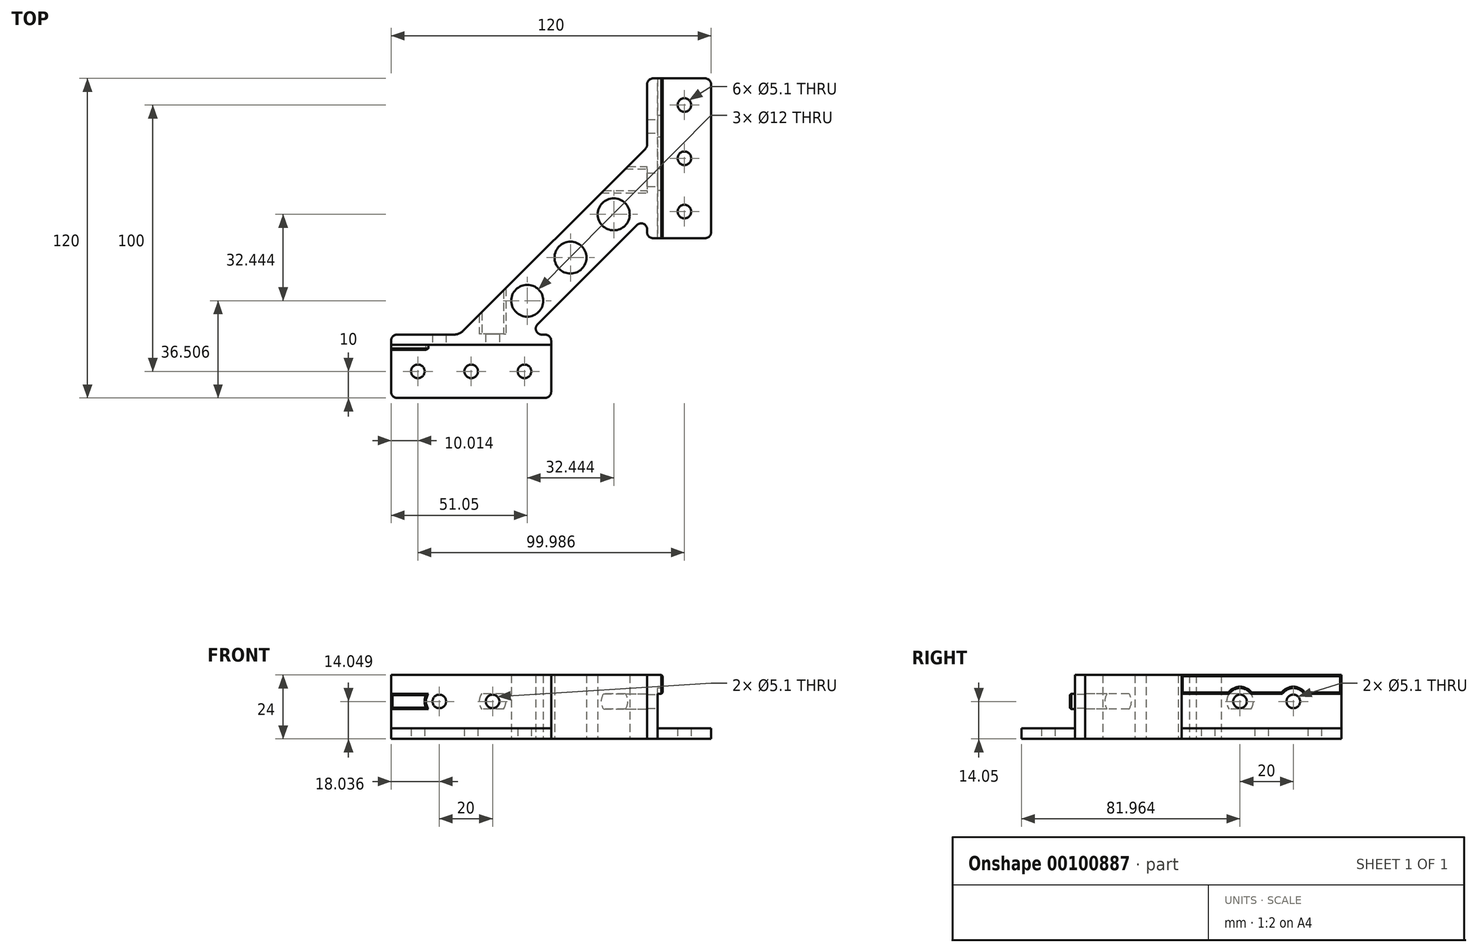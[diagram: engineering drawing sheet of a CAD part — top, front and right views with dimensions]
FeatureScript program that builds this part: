
annotation { "Feature Type Name" : "Feature", "Feature Type Description" : "" }
export const myFeature = defineFeature(function(context is Context, id is Id, definition is map)
    precondition{}
    {
        {
            var Q0;
            Q0=qCreatedBy(makeId("Top.planeOp"),FACE);
            var sketch = newSketch(context, id + "F0", { "sketchPlane" : qUnion([Q0])});
            skLineSegment(sketch, "E0", {"start": v(72.19, 64.92) * mm, "end": v(34.9, 27.62) * mm});
            skLineSegment(sketch, "E1", {"start": v(75.35, 93.53) * mm, "end": v(7.1, 25.27) * mm});
            skLineSegment(sketch, "E2", {"start": v(90, 80) * mm, "end": v(90, 70) * mm, "construction": true});
            skLineSegment(sketch, "E3", {"start": v(90, 80) * mm, "end": v(90, 90) * mm, "construction": true});
            skCircle(sketch, "E4", {"center": v(90, 90) * mm, "radius": 2.55 * mm});
            skCircle(sketch, "E5", {"center": v(90, 70) * mm, "radius": 2.55 * mm});
            skLineSegment(sketch, "E6", {"start": v(20.01, 10) * mm, "end": v(10.01, 10) * mm, "construction": true});
            skLineSegment(sketch, "E7", {"start": v(20.01, 10) * mm, "end": v(30.01, 10) * mm, "construction": true});
            skCircle(sketch, "E8", {"center": v(30.01, 10) * mm, "radius": 2.55 * mm});
            skCircle(sketch, "E9", {"center": v(10.01, 10) * mm, "radius": 2.55 * mm});
            skLineSegment(sketch, "E10", {"start": v(80, 92.8) * mm, "end": v(80, 73.96) * mm});
            skLineSegment(sketch, "E11", {"start": v(7.2, 20) * mm, "end": v(26.04, 20) * mm});
            skCircle(sketch, "E12", {"center": v(31.05, 36.5) * mm, "radius": 6 * mm});
            skCircle(sketch, "E13", {"center": v(63.5, 68.95) * mm, "radius": 6 * mm});
            skCircle(sketch, "E14", {"center": v(47.27, 52.73) * mm, "radius": 6 * mm});
            skPoint(sketch, "E15.visualSharp", {"position": v(0, 0) * mm});
            skPoint(sketch, "E16.visualSharp", {"position": v(40, 0) * mm});
            skArc(sketch, "E16.filletArc", {"start": v(37.77, 0) * mm, "mid": v(39.35, 0.65) * mm, "end": v(40, 2.23) * mm});
            skPoint(sketch, "E17.visualSharp", {"position": v(40, 20) * mm});
            skPoint(sketch, "E18.visualSharp", {"position": v(100, 60) * mm});
            skArc(sketch, "E18.filletArc", {"start": v(97.77, 60) * mm, "mid": v(99.35, 60.65) * mm, "end": v(100, 62.23) * mm});
            skPoint(sketch, "E19.visualSharp", {"position": v(80, 60) * mm});
            skArc(sketch, "E20.filletArc", {"start": v(79.42, 72.46) * mm, "mid": v(79.85, 73.16) * mm, "end": v(80, 73.96) * mm});
            skLineSegment(sketch, "E21", {"start": v(80, 60) * mm, "end": v(40, 20) * mm, "construction": true});
            skLineSegment(sketch, "E22", {"start": v(63.5, 68.95) * mm, "end": v(57.13, 75.31) * mm, "construction": true});
            skLineSegment(sketch, "E23", {"start": v(47.27, 52.73) * mm, "end": v(40.9, 59.1) * mm, "construction": true});
            skLineSegment(sketch, "E24", {"start": v(31.05, 36.5) * mm, "end": v(24.69, 42.87) * mm, "construction": true});
            skLineSegment(sketch, "E25", {"start": v(40, 0) * mm, "end": v(-17.77, 0) * mm});
            skLineSegment(sketch, "E26", {"start": v(-20, 2.23) * mm, "end": v(-20, 20) * mm});
            skLineSegment(sketch, "E27", {"start": v(-20, 20) * mm, "end": v(7.2, 20) * mm});
            skLineSegment(sketch, "E28", {"start": v(10.01, 10) * mm, "end": v(-9.99, 10) * mm, "construction": true});
            skCircle(sketch, "E29", {"center": v(-9.99, 10) * mm, "radius": 2.55 * mm});
            skLineSegment(sketch, "E30", {"start": v(3.56, 23.8) * mm, "end": v(-17.77, 23.8) * mm});
            skLineSegment(sketch, "E31", {"start": v(-20, 21.58) * mm, "end": v(-20, 20) * mm});
            skArc(sketch, "E32.filletArc", {"start": v(3.56, 23.8) * mm, "mid": v(5.47, 24.2) * mm, "end": v(7.1, 25.27) * mm});
            skPoint(sketch, "E33.visualSharp", {"position": v(-20, 23.8) * mm});
            skArc(sketch, "E33.filletArc", {"start": v(-17.77, 23.8) * mm, "mid": v(-19.35, 23.16) * mm, "end": v(-20, 21.58) * mm});
            skPoint(sketch, "E34.visualSharp", {"position": v(-20, 0) * mm});
            skArc(sketch, "E34.filletArc", {"start": v(-20, 2.23) * mm, "mid": v(-19.35, 0.65) * mm, "end": v(-17.77, 0) * mm});
            skLineSegment(sketch, "E35", {"start": v(36.47, 23.8) * mm, "end": v(37.77, 23.8) * mm});
            skLineSegment(sketch, "E36", {"start": v(40, 2.23) * mm, "end": v(40, 21.58) * mm});
            skPoint(sketch, "E37.visualSharp", {"position": v(40, 23.8) * mm});
            skArc(sketch, "E37.filletArc", {"start": v(40, 21.58) * mm, "mid": v(39.35, 23.16) * mm, "end": v(37.77, 23.8) * mm});
            skArc(sketch, "E38.filletArc", {"start": v(34.9, 27.62) * mm, "mid": v(34.4, 25.19) * mm, "end": v(36.47, 23.8) * mm});
            skLineSegment(sketch, "E39", {"start": v(40, 20) * mm, "end": v(26.04, 20) * mm});
            skLineSegment(sketch, "E40", {"start": v(97.77, 120) * mm, "end": v(82.23, 120) * mm});
            skLineSegment(sketch, "E41", {"start": v(80, 117.77) * mm, "end": v(80, 92.8) * mm});
            skLineSegment(sketch, "E42", {"start": v(80, 120) * mm, "end": v(78.23, 120) * mm});
            skLineSegment(sketch, "E43", {"start": v(76, 117.77) * mm, "end": v(76, 95.1) * mm});
            skLineSegment(sketch, "E44", {"start": v(100, 117.77) * mm, "end": v(100, 62.23) * mm});
            skPoint(sketch, "E45.visualSharp", {"position": v(100, 120) * mm});
            skArc(sketch, "E45.filletArc", {"start": v(100, 117.77) * mm, "mid": v(99.35, 119.35) * mm, "end": v(97.77, 120) * mm});
            skPoint(sketch, "E46.visualSharp", {"position": v(80, 120) * mm});
            skPoint(sketch, "E47.visualSharp", {"position": v(76, 120) * mm});
            skArc(sketch, "E47.filletArc", {"start": v(78.23, 120) * mm, "mid": v(76.65, 119.35) * mm, "end": v(76, 117.77) * mm});
            skPoint(sketch, "E48.newPointB", {"position": v(76.2, 94.37) * mm});
            skArc(sketch, "E48.filletArc", {"start": v(75.35, 93.53) * mm, "mid": v(75.83, 94.25) * mm, "end": v(76, 95.1) * mm});
            skLineSegment(sketch, "E49", {"start": v(80, 120) * mm, "end": v(82.23, 120) * mm});
            skLineSegment(sketch, "E50", {"start": v(80, 117.77) * mm, "end": v(80, 120) * mm});
            skLineSegment(sketch, "E51", {"start": v(90, 90) * mm, "end": v(90, 110) * mm, "construction": true});
            skCircle(sketch, "E52", {"center": v(90, 110) * mm, "radius": 2.55 * mm});
            skLineSegment(sketch, "E53", {"start": v(97.77, 60) * mm, "end": v(78.23, 60) * mm});
            skLineSegment(sketch, "E54", {"start": v(76, 62.23) * mm, "end": v(76, 63.34) * mm});
            skPoint(sketch, "E55.visualSharp", {"position": v(76, 60) * mm});
            skArc(sketch, "E55.filletArc", {"start": v(76, 62.23) * mm, "mid": v(76.65, 60.65) * mm, "end": v(78.23, 60) * mm});
            skLineSegment(sketch, "E56", {"start": v(80, 73.96) * mm, "end": v(80, 60) * mm});
            skArc(sketch, "E57.filletArc", {"start": v(76, 63.34) * mm, "mid": v(74.62, 65.4) * mm, "end": v(72.19, 64.92) * mm});
            skSolve(sketch);
        }
        {
            var Q0;
            Q0=makeQuery(id+"F0.imprint","IMPRINT",FACE,{"disambiguationData":[TD([[makeQuery(id+"F0.imprint","IMPRINT",EDGE,{"derivedFrom":sQuery(id+"F0.wireOp",EDGE,"vu9Mk9B3-tYnc-hBh3-YSRa-gffN2kaJFWOu.bottom")}),1.0]])]});
            var Q1;
            Q1=makeQuery(id+"F0.imprint","IMPRINT",FACE,{"disambiguationData":[TD([[makeQuery(id+"F0.imprint","IMPRINT",EDGE,{"derivedFrom":sQuery(id+"F0.wireOp",EDGE,"dHSvPDMb-Tlqj-Q4RQ-VTB6-cDBXFjwvFFpO.bottom")}),1.0]])]});
            var Q2;
            Q2=makeQuery(id+"F0.imprint","IMPRINT",FACE,{"disambiguationData":[TD([[makeQuery(id+"F0.imprint","IMPRINT",EDGE,{"derivedFrom":sQuery(id+"F0.wireOp",EDGE,"vu9Mk9B3-tYnc-hBh3-YSRa-gffN2kaJFWOu.top")}),-1.0]])]});
            var Q3;
            Q3=makeQuery(id+"F0.imprint","IMPRINT",FACE,{"disambiguationData":[TD([[makeQuery(id+"F0.imprint","IMPRINT",EDGE,{"derivedFrom":sQuery(id+"F0.wireOp",EDGE,"dfbe4f2e-9168-4a66-9229-19b176851153.filletArc")}),-1.0]])]});
            var Q4;
            Q4=makeQuery(id+"F0.imprint","IMPRINT",FACE,{"disambiguationData":[TD([[makeQuery(id+"F0.imprint","IMPRINT",EDGE,{"derivedFrom":sQuery(id+"F0.wireOp",EDGE,"E8")}),-1.0]])]});
            var Q5;
            Q5=makeQuery(id+"F0.imprint","IMPRINT",FACE,{"disambiguationData":[TD([[makeQuery(id+"F0.imprint","IMPRINT",EDGE,{"derivedFrom":sQuery(id+"F0.wireOp",EDGE,"dHSvPDMb-Tlqj-Q4RQ-VTB6-cDBXFjwvFFpO.top")}),-1.0]])]});
            var Q6;
            Q6=makeQuery(id+"F0.imprint","IMPRINT",FACE,{"disambiguationData":[TD([[makeQuery(id+"F0.imprint","IMPRINT",EDGE,{"derivedFrom":sQuery(id+"F0.wireOp",EDGE,"d131ca40-41fb-4f96-a70f-9a93196c1724.filletArc")}),-1.0]])]});
            var Q7;
            Q7=makeQuery(id+"F0.imprint","IMPRINT",FACE,{"disambiguationData":[TD([[makeQuery(id+"F0.imprint","IMPRINT",EDGE,{"derivedFrom":sQuery(id+"F0.wireOp",EDGE,"E4")}),-1.0]])]});
            extrude(context, id + "F1", {"entities" : qUnion([Q0, Q1, Q2, Q3, Q4, Q5, Q6, Q7]), "depth" : 4 * mm});
        }
        {
            var Q0;
            Q0=makeQuery(id+"F0.imprint","IMPRINT",FACE,{"disambiguationData":[TD([[makeQuery(id+"F0.imprint","IMPRINT",EDGE,{"derivedFrom":sQuery(id+"F0.wireOp",EDGE,"E0")}),-1.0]])]});
            var Q1;
            Q1=makeQuery(id+"F0.imprint","IMPRINT",FACE,{"disambiguationData":[TD([[makeQuery(id+"F0.imprint","IMPRINT",EDGE,{"derivedFrom":sQuery(id+"F0.wireOp",EDGE,"dfbe4f2e-9168-4a66-9229-19b176851153.filletArc")}),-1.0]])]});
            var Q2;
            Q2=makeQuery(id+"F0.imprint","IMPRINT",FACE,{"disambiguationData":[TD([[makeQuery(id+"F0.imprint","IMPRINT",EDGE,{"derivedFrom":sQuery(id+"F0.wireOp",EDGE,"E35")}),-1.0]])]});
            var Q3;
            Q3=makeQuery(id+"F0.imprint","IMPRINT",FACE,{"disambiguationData":[TD([[makeQuery(id+"F0.imprint","IMPRINT",EDGE,{"derivedFrom":sQuery(id+"F0.wireOp",EDGE,"d131ca40-41fb-4f96-a70f-9a93196c1724.filletArc")}),-1.0]])]});
            extrude(context, id + "F2", {"entities" : qUnion([Q0, Q1, Q2, Q3]), "depth" : 24 * mm});
        }
        {
            var Q0;
            Q0=makeQuery(id+"F2.opExtrude","SWEPT_FACE",FACE,{"disambiguationData":[OSD([sQuery(id+"F0.wireOp",EDGE,"E10")])]});
            var sketch = newSketch(context, id + "F3", { "sketchPlane" : qUnion([Q0])});
            skCircle(sketch, "E58", {"center": v(81.96, 14.05) * mm, "radius": 2.55 * mm});
            skCircle(sketch, "E59", {"center": v(81.96, 14.05) * mm, "radius": 5 * mm});
            skLineSegment(sketch, "E60", {"start": v(75.68, 14.05) * mm, "end": v(75.68, 16.95) * mm, "construction": true});
            skLineSegment(sketch, "E61", {"start": v(75.68, 14.05) * mm, "end": v(75.68, 11.15) * mm, "construction": true});
            skLineSegment(sketch, "E62.bottom", {"start": v(84.86, 11.15) * mm, "end": v(79.06, 11.15) * mm});
            skLineSegment(sketch, "E62.top", {"start": v(84.86, 16.95) * mm, "end": v(79.06, 16.95) * mm});
            skLineSegment(sketch, "E62.left", {"start": v(84.86, 11.15) * mm, "end": v(84.86, 16.95) * mm});
            skLineSegment(sketch, "E62.right", {"start": v(79.06, 11.15) * mm, "end": v(79.06, 16.95) * mm});
            skLineSegment(sketch, "E63", {"start": v(60, 16.95) * mm, "end": v(120, 16.95) * mm});
            skLineSegment(sketch, "E64", {"start": v(60, 11.15) * mm, "end": v(120, 11.15) * mm});
            skLineSegment(sketch, "E65", {"start": v(81.96, 14.05) * mm, "end": v(101.96, 14.05) * mm, "construction": true});
            skLineSegment(sketch, "E66", {"start": v(81.96, 14.05) * mm, "end": v(60, 14.05) * mm, "construction": true});
            skCircle(sketch, "E67", {"center": v(101.96, 14.05) * mm, "radius": 2.55 * mm});
            skLineSegment(sketch, "E68.bottom", {"start": v(104.86, 11.15) * mm, "end": v(99.06, 11.15) * mm});
            skLineSegment(sketch, "E68.top", {"start": v(104.86, 16.95) * mm, "end": v(99.06, 16.95) * mm});
            skLineSegment(sketch, "E68.left", {"start": v(104.86, 11.15) * mm, "end": v(104.86, 16.95) * mm});
            skLineSegment(sketch, "E68.right", {"start": v(99.06, 11.15) * mm, "end": v(99.06, 16.95) * mm});
            skCircle(sketch, "E69", {"center": v(101.96, 14.05) * mm, "radius": 5 * mm});
            skSolve(sketch);
        }
        {
            var Q0;
            Q0=makeQuery(id+"F3.imprint","IMPRINT",FACE,{"disambiguationData":[TD([[makeQuery(id+"F3.imprint","IMPRINT",EDGE,{"derivedFrom":sQuery(id+"F3.wireOp",EDGE,"E58")}),1.0]])]});
            var Q1;
            Q1=makeQuery(id+"F3.imprint","IMPRINT",FACE,{"disambiguationData":[TD([[makeQuery(id+"F3.imprint","IMPRINT",EDGE,{"derivedFrom":sQuery(id+"F3.wireOp",EDGE,"E67")}),1.0]])]});
            extrude(context, id + "F4", {"entities" : qUnion([Q0, Q1]), "operationType" : NewBodyOperationType.REMOVE, "oppositeDirection" : true, "depth" : 25 * mm});
        }
        {
            var Q0;
            Q0=makeQuery(id+"F3.imprint","IMPRINT",FACE,{"disambiguationData":[TD([[makeQuery(id+"F3.imprint","IMPRINT",EDGE,{"derivedFrom":sQuery(id+"F3.wireOp",EDGE,"E58")}),-1.0]])]});
            var Q1;
            {var subQ0=sQuery(id+"F3.wireOp",EDGE,"jhnVX4wI-j8lZ-3AVm-xeLm-CdO5rJdbQkBP");var subQ1=sQuery(id+"F3.wireOp",EDGE,"E59");var subQ2=makeQuery(id+"F3.imprint","INTERSECT",VERTEX,{"disambiguationData":[OD(0.0)],"derivedFrom":[subQ1,subQ0]});Q1=makeQuery(id+"F3.imprint","IMPRINT",FACE,{"disambiguationData":[TD([[makeQuery(id+"F3.imprint","IMPRINT",EDGE,{"disambiguationData":[TD([[subQ2,1.0]])],"derivedFrom":subQ1}),1.0]])]});}
            var Q2;
            {var subQ0=sQuery(id+"F3.wireOp",EDGE,"Id8RdnPz-wRiC-AdUC-IpGY-bHKos9TCPgaF");var subQ1=sQuery(id+"F3.wireOp",EDGE,"E59");var subQ2=makeQuery(id+"F3.imprint","INTERSECT",VERTEX,{"disambiguationData":[OD(0.0)],"derivedFrom":[subQ1,subQ0]});Q2=makeQuery(id+"F3.imprint","IMPRINT",FACE,{"disambiguationData":[TD([[makeQuery(id+"F3.imprint","IMPRINT",EDGE,{"disambiguationData":[TD([[subQ2,-1.0]])],"derivedFrom":subQ1}),1.0]])]});}
            var Q3;
            {var subQ5=sQuery(id+"F3.wireOp",EDGE,"E62.right");Q3=makeQuery(id+"F3.imprint","IMPRINT",FACE,{"disambiguationData":[TD([[makeQuery(id+"F3.imprint","IMPRINT",EDGE,{"derivedFrom":subQ5}),1.0]])]});}
            var Q4;
            {var subQ5=sQuery(id+"F3.wireOp",EDGE,"E62.left");Q4=makeQuery(id+"F3.imprint","IMPRINT",FACE,{"disambiguationData":[TD([[makeQuery(id+"F3.imprint","IMPRINT",EDGE,{"derivedFrom":subQ5}),-1.0]])]});}
            extrude(context, id + "F5", {"entities" : qUnion([Q0, Q1, Q2, Q3, Q4]), "operationType" : NewBodyOperationType.REMOVE, "oppositeDirection" : true, "depth" : 25 * mm, "hasSecondDirection" : true, "secondDirectionOppositeDirection" : true, "secondDirectionDepth" : 4 * mm});
        }
        {
            var Q0;
            {var subQ0=sQuery(id+"F3.wireOp",EDGE,"jhnVX4wI-j8lZ-3AVm-xeLm-CdO5rJdbQkBP");var subQ1=sQuery(id+"F3.wireOp",EDGE,"E59");var subQ2=makeQuery(id+"F3.imprint","INTERSECT",VERTEX,{"disambiguationData":[OD(0.0)],"derivedFrom":[subQ1,subQ0]});Q0=makeQuery(id+"F3.imprint","IMPRINT",FACE,{"disambiguationData":[TD([[makeQuery(id+"F3.imprint","IMPRINT",EDGE,{"disambiguationData":[TD([[subQ2,-1.0]])],"derivedFrom":subQ1}),-1.0]])]});}
            var Q1;
            {var subQ0=sQuery(id+"F3.wireOp",EDGE,"jhnVX4wI-j8lZ-3AVm-xeLm-CdO5rJdbQkBP");var subQ1=sQuery(id+"F3.wireOp",EDGE,"E59");var subQ2=makeQuery(id+"F3.imprint","INTERSECT",VERTEX,{"disambiguationData":[OD(1.0)],"derivedFrom":[subQ1,subQ0]});Q1=makeQuery(id+"F3.imprint","IMPRINT",FACE,{"disambiguationData":[TD([[makeQuery(id+"F3.imprint","IMPRINT",EDGE,{"disambiguationData":[TD([[subQ2,1.0]])],"derivedFrom":subQ1}),-1.0]])]});}
            var Q2;
            {var subQ0=sQuery(id+"F3.wireOp",EDGE,"E63");var subQ3=sQuery(id+"F3.wireOp",EDGE,"E69");var subQ4=makeQuery(id+"F3.imprint","INTERSECT",VERTEX,{"disambiguationData":[OD(1.0)],"derivedFrom":[subQ0,subQ3]});Q2=makeQuery(id+"F3.imprint","IMPRINT",FACE,{"disambiguationData":[TD([[makeQuery(id+"F3.imprint","IMPRINT",EDGE,{"disambiguationData":[TD([[subQ4,1.0]])],"derivedFrom":subQ3}),-1.0]])]});}
            extrude(context, id + "F6", {"entities" : qUnion([Q0, Q1, Q2]), "operationType" : NewBodyOperationType.ADD, "depth" : 1.9 * mm});
        }
        {
            var Q0;
            Q0=makeQuery(id+"F2.opExtrude","SWEPT_FACE",FACE,{"disambiguationData":[OSD([sQuery(id+"F0.wireOp",EDGE,"E11")])]});
            var sketch = newSketch(context, id + "F7", { "sketchPlane" : qUnion([Q0])});
            skLineSegment(sketch, "E70", {"start": v(18.04, 14.05) * mm, "end": v(26.04, 14.04) * mm, "construction": true});
            skCircle(sketch, "E71", {"center": v(18.04, 14.05) * mm, "radius": 2.55 * mm});
            skCircle(sketch, "E72", {"center": v(18.04, 14.05) * mm, "radius": 5 * mm});
            skLineSegment(sketch, "E73", {"start": v(28.9, 14.04) * mm, "end": v(28.9, 16.94) * mm, "construction": true});
            skLineSegment(sketch, "E74", {"start": v(25.05, 14.04) * mm, "end": v(25.05, 11.14) * mm, "construction": true});
            skLineSegment(sketch, "E75.bottom", {"start": v(20.94, 11.14) * mm, "end": v(15.14, 11.14) * mm});
            skLineSegment(sketch, "E75.top", {"start": v(20.94, 16.96) * mm, "end": v(15.14, 16.96) * mm});
            skLineSegment(sketch, "E75.left", {"start": v(20.94, 11.14) * mm, "end": v(20.94, 16.96) * mm});
            skLineSegment(sketch, "E75.right", {"start": v(15.14, 11.14) * mm, "end": v(15.14, 16.96) * mm});
            skLineSegment(sketch, "E76", {"start": v(18.04, 14.05) * mm, "end": v(-1.96, 14.05) * mm, "construction": true});
            skCircle(sketch, "E77", {"center": v(-1.96, 14.05) * mm, "radius": 2.55 * mm});
            skCircle(sketch, "E78", {"center": v(-1.96, 14.05) * mm, "radius": 5 * mm});
            skLineSegment(sketch, "E79.bottom", {"start": v(0.94, 11.14) * mm, "end": v(-4.86, 11.14) * mm});
            skLineSegment(sketch, "E79.top", {"start": v(0.94, 16.96) * mm, "end": v(-4.86, 16.96) * mm});
            skLineSegment(sketch, "E79.left", {"start": v(0.94, 11.14) * mm, "end": v(0.94, 16.96) * mm});
            skLineSegment(sketch, "E79.right", {"start": v(-4.86, 11.14) * mm, "end": v(-4.86, 16.96) * mm});
            skLineSegment(sketch, "E80", {"start": v(-20, 11.14) * mm, "end": v(40, 11.14) * mm});
            skLineSegment(sketch, "E81", {"start": v(40, 16.96) * mm, "end": v(-20, 16.96) * mm});
            skSolve(sketch);
        }
        {
            var Q0;
            Q0=makeQuery(id+"F7.imprint","IMPRINT",FACE,{"disambiguationData":[TD([[makeQuery(id+"F7.imprint","IMPRINT",EDGE,{"derivedFrom":sQuery(id+"F7.wireOp",EDGE,"E71")}),1.0]])]});
            var Q1;
            Q1=makeQuery(id+"F7.imprint","IMPRINT",FACE,{"disambiguationData":[TD([[makeQuery(id+"F7.imprint","IMPRINT",EDGE,{"derivedFrom":sQuery(id+"F7.wireOp",EDGE,"E77")}),1.0]])]});
            extrude(context, id + "F8", {"entities" : qUnion([Q0, Q1]), "operationType" : NewBodyOperationType.REMOVE, "oppositeDirection" : true, "depth" : 22.92 * mm});
        }
        {
            var Q0;
            Q0=makeQuery(id+"F7.imprint","IMPRINT",FACE,{"disambiguationData":[TD([[makeQuery(id+"F7.imprint","IMPRINT",EDGE,{"derivedFrom":sQuery(id+"F7.wireOp",EDGE,"E71")}),-1.0]])]});
            var Q1;
            {var subQ0=sQuery(id+"F7.wireOp",EDGE,"eQdLDAcd-6LPi-2LcR-mTip-Mz5f3yXqDBEm");var subQ1=sQuery(id+"F7.wireOp",EDGE,"E72");var subQ2=makeQuery(id+"F7.imprint","INTERSECT",VERTEX,{"disambiguationData":[OD(0.0)],"derivedFrom":[subQ1,subQ0]});Q1=makeQuery(id+"F7.imprint","IMPRINT",FACE,{"disambiguationData":[TD([[makeQuery(id+"F7.imprint","IMPRINT",EDGE,{"disambiguationData":[TD([[subQ2,1.0]])],"derivedFrom":subQ1}),1.0]])]});}
            var Q2;
            {var subQ0=sQuery(id+"F7.wireOp",EDGE,"vgkWriN9-ka4X-9NQ1-BzAB-JLWM9luxvIlH");var subQ1=sQuery(id+"F7.wireOp",EDGE,"E72");var subQ2=makeQuery(id+"F7.imprint","INTERSECT",VERTEX,{"disambiguationData":[OD(0.0)],"derivedFrom":[subQ1,subQ0]});Q2=makeQuery(id+"F7.imprint","IMPRINT",FACE,{"disambiguationData":[TD([[makeQuery(id+"F7.imprint","IMPRINT",EDGE,{"disambiguationData":[TD([[subQ2,-1.0]])],"derivedFrom":subQ1}),1.0]])]});}
            var Q3;
            {var subQ5=sQuery(id+"F7.wireOp",EDGE,"E75.right");Q3=makeQuery(id+"F7.imprint","IMPRINT",FACE,{"disambiguationData":[TD([[makeQuery(id+"F7.imprint","IMPRINT",EDGE,{"derivedFrom":subQ5}),1.0]])]});}
            var Q4;
            {var subQ5=sQuery(id+"F7.wireOp",EDGE,"E75.left");Q4=makeQuery(id+"F7.imprint","IMPRINT",FACE,{"disambiguationData":[TD([[makeQuery(id+"F7.imprint","IMPRINT",EDGE,{"derivedFrom":subQ5}),-1.0]])]});}
            extrude(context, id + "F9", {"entities" : qUnion([Q0, Q1, Q2, Q3, Q4]), "operationType" : NewBodyOperationType.REMOVE, "oppositeDirection" : true, "depth" : 25 * mm, "hasSecondDirection" : true, "secondDirectionOppositeDirection" : true, "secondDirectionDepth" : 4 * mm});
        }
        {
            var Q0;
            {var subQ0=sQuery(id+"F7.wireOp",EDGE,"eQdLDAcd-6LPi-2LcR-mTip-Mz5f3yXqDBEm");var subQ1=sQuery(id+"F7.wireOp",EDGE,"E72");var subQ2=makeQuery(id+"F7.imprint","INTERSECT",VERTEX,{"disambiguationData":[OD(0.0)],"derivedFrom":[subQ1,subQ0]});Q0=makeQuery(id+"F7.imprint","IMPRINT",FACE,{"disambiguationData":[TD([[makeQuery(id+"F7.imprint","IMPRINT",EDGE,{"disambiguationData":[TD([[subQ2,-1.0]])],"derivedFrom":subQ1}),-1.0]])]});}
            var Q1;
            {var subQ0=sQuery(id+"F7.wireOp",EDGE,"eQdLDAcd-6LPi-2LcR-mTip-Mz5f3yXqDBEm");var subQ1=sQuery(id+"F7.wireOp",EDGE,"E72");var subQ2=makeQuery(id+"F7.imprint","INTERSECT",VERTEX,{"disambiguationData":[OD(1.0)],"derivedFrom":[subQ1,subQ0]});Q1=makeQuery(id+"F7.imprint","IMPRINT",FACE,{"disambiguationData":[TD([[makeQuery(id+"F7.imprint","IMPRINT",EDGE,{"disambiguationData":[TD([[subQ2,1.0]])],"derivedFrom":subQ1}),-1.0]])]});}
            var Q2;
            {var subQ0=sQuery(id+"F7.wireOp",EDGE,"00ev6eyV-6F4C-Ywux-UBGc-KEgbBK6Ml0yh");var subQ3=sQuery(id+"F7.wireOp",EDGE,"E78");var subQ4=makeQuery(id+"F7.imprint","INTERSECT",VERTEX,{"disambiguationData":[OD(1.0)],"derivedFrom":[subQ0,subQ3]});Q2=makeQuery(id+"F7.imprint","IMPRINT",FACE,{"disambiguationData":[TD([[makeQuery(id+"F7.imprint","IMPRINT",EDGE,{"disambiguationData":[TD([[subQ4,-1.0]])],"derivedFrom":subQ3}),-1.0]])]});}
            var Q3;
            {var subQ0=sQuery(id+"F7.wireOp",EDGE,"E81");var subQ1=sQuery(id+"F7.wireOp",EDGE,"E78");var subQ2=makeQuery(id+"F7.imprint","INTERSECT",VERTEX,{"disambiguationData":[OD(0.0)],"derivedFrom":[subQ1,subQ0]});Q3=makeQuery(id+"F7.imprint","IMPRINT",FACE,{"disambiguationData":[TD([[makeQuery(id+"F7.imprint","IMPRINT",EDGE,{"disambiguationData":[TD([[subQ2,-1.0]])],"derivedFrom":subQ1}),-1.0]])]});}
            extrude(context, id + "F10", {"entities" : qUnion([Q0, Q1, Q2, Q3]), "operationType" : NewBodyOperationType.ADD, "depth" : 1.9 * mm});
        }
        {
            var Q0;
            Q0=makeQuery(id+"F10.opExtrude","CAP_FACE",FACE,{"disambiguationData":[OSD([sQuery(id+"F0.wireOp",EDGE,"E11"),sQuery(id+"F0.wireOp",EDGE,"8db506b6-ee8a-469c-9ccc-82291fc62510.filletArc"),sQuery(id+"F0.wireOp",EDGE,"dfbe4f2e-9168-4a66-9229-19b176851153.filletArc"),sQuery(id+"F7.wireOp",EDGE,"E71"),sQuery(id+"F7.wireOp",EDGE,"eQdLDAcd-6LPi-2LcR-mTip-Mz5f3yXqDBEm"),sQuery(id+"F7.wireOp",EDGE,"vgkWriN9-ka4X-9NQ1-BzAB-JLWM9luxvIlH")])],"isStart":false});
            var Q1;
            Q1=makeQuery(id+"F6.opExtrude","CAP_FACE",FACE,{"disambiguationData":[OSD([sQuery(id+"F0.wireOp",EDGE,"E10"),sQuery(id+"F0.wireOp",EDGE,"d131ca40-41fb-4f96-a70f-9a93196c1724.filletArc"),sQuery(id+"F0.wireOp",EDGE,"E20.filletArc"),sQuery(id+"F3.wireOp",EDGE,"E58"),sQuery(id+"F3.wireOp",EDGE,"Id8RdnPz-wRiC-AdUC-IpGY-bHKos9TCPgaF"),sQuery(id+"F3.wireOp",EDGE,"jhnVX4wI-j8lZ-3AVm-xeLm-CdO5rJdbQkBP")])],"isStart":false});
            var Q2;
            Q2=makeQuery(id+"F10.opExtrude","CAP_FACE",FACE,{"disambiguationData":[OSD([sQuery(id+"F0.wireOp",EDGE,"E26"),sQuery(id+"F0.wireOp",EDGE,"E27"),sQuery(id+"F0.wireOp",EDGE,"E31"),sQuery(id+"F7.wireOp",EDGE,"E72"),sQuery(id+"F7.wireOp",EDGE,"00ev6eyV-6F4C-Ywux-UBGc-KEgbBK6Ml0yh"),sQuery(id+"F7.wireOp",EDGE,"TnYP78Dp-XoBh-2oav-cX5g-tvHuRymN2nPa")])],"isStart":false});
            var Q3;
            Q3=makeQuery(id+"F10.opExtrude","CAP_FACE",FACE,{"disambiguationData":[OSD([sQuery(id+"F7.wireOp",EDGE,"E72"),sQuery(id+"F7.wireOp",EDGE,"00ev6eyV-6F4C-Ywux-UBGc-KEgbBK6Ml0yh"),sQuery(id+"F7.wireOp",EDGE,"TnYP78Dp-XoBh-2oav-cX5g-tvHuRymN2nPa"),sQuery(id+"F7.wireOp",EDGE,"E78")])],"isStart":false});
            var Q4;
            Q4=makeQuery(id+"F10.opExtrude","CAP_FACE",FACE,{"disambiguationData":[OSD([sQuery(id+"F0.wireOp",EDGE,"E36"),sQuery(id+"F0.wireOp",EDGE,"E39"),sQuery(id+"F7.wireOp",EDGE,"E72"),sQuery(id+"F7.wireOp",EDGE,"E80"),sQuery(id+"F7.wireOp",EDGE,"E81")])],"isStart":false});
            var Q5;
            Q5=makeQuery(id+"F6.opExtrude","CAP_FACE",FACE,{"disambiguationData":[OSD([sQuery(id+"F0.wireOp",EDGE,"E53"),sQuery(id+"F0.wireOp",EDGE,"E56"),sQuery(id+"F3.wireOp",EDGE,"E59"),sQuery(id+"F3.wireOp",EDGE,"E63"),sQuery(id+"F3.wireOp",EDGE,"E64")])],"isStart":false});
            var Q6;
            Q6=makeQuery(id+"F6.opExtrude","CAP_FACE",FACE,{"disambiguationData":[OSD([sQuery(id+"F3.wireOp",EDGE,"E59"),sQuery(id+"F3.wireOp",EDGE,"E63"),sQuery(id+"F3.wireOp",EDGE,"E64"),sQuery(id+"F3.wireOp",EDGE,"E69")])],"isStart":false});
            var Q7;
            Q7=makeQuery(id+"F6.opExtrude","CAP_FACE",FACE,{"disambiguationData":[OSD([sQuery(id+"F0.wireOp",EDGE,"E42"),sQuery(id+"F0.wireOp",EDGE,"E49"),sQuery(id+"F0.wireOp",EDGE,"E50"),sQuery(id+"F3.wireOp",EDGE,"E63"),sQuery(id+"F3.wireOp",EDGE,"E64"),sQuery(id+"F3.wireOp",EDGE,"E69")])],"isStart":false});
            chamfer(context, id + "F11", {"entities" : qUnion([Q0, Q1, Q2, Q3, Q4, Q5, Q6, Q7]), "width" : .5 * mm, "tangentPropagation" : true});
        }
    });
